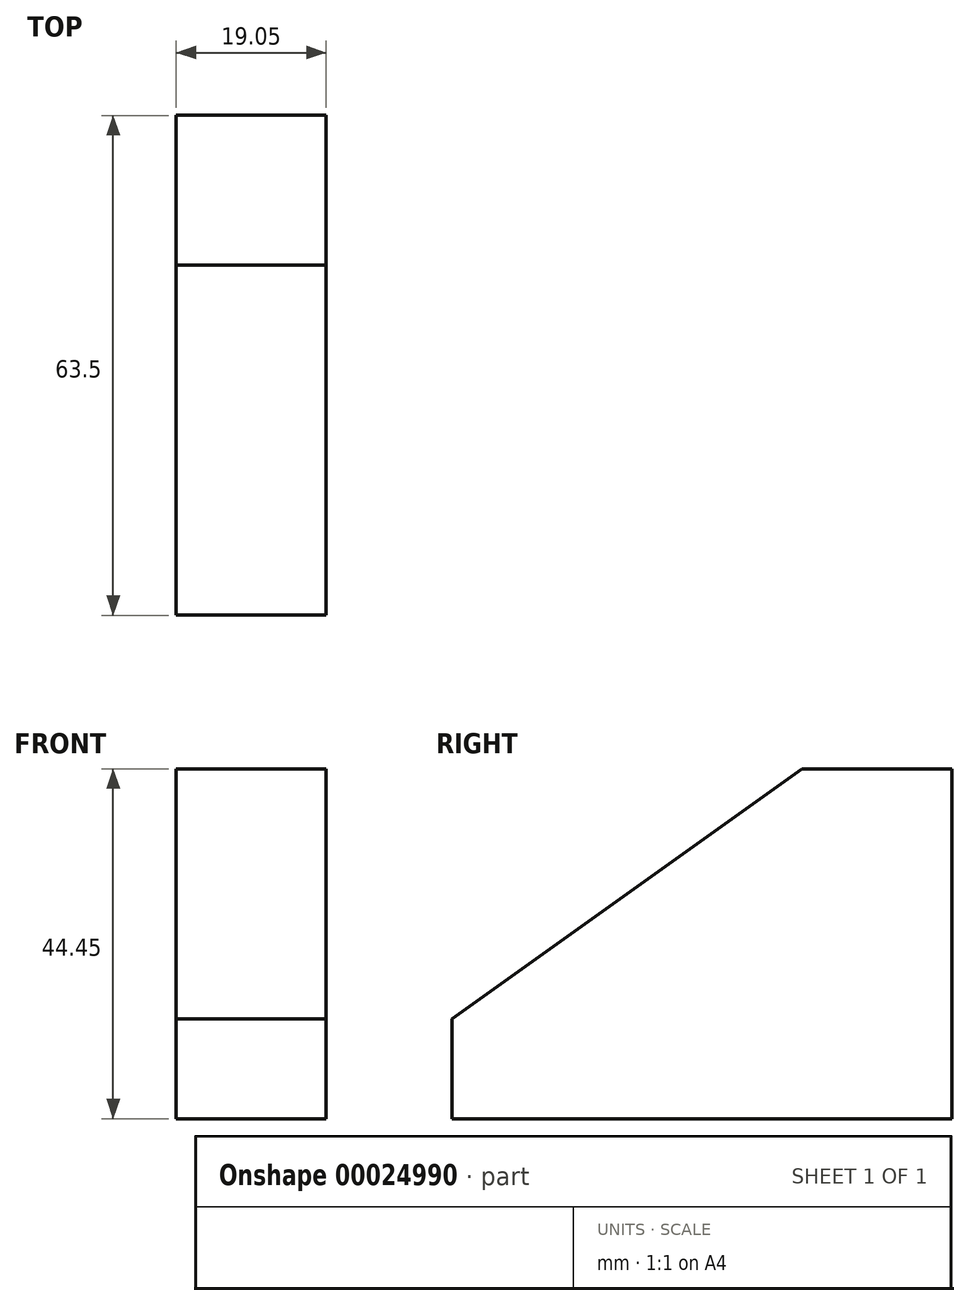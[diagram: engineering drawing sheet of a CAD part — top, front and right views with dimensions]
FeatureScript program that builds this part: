
annotation { "Feature Type Name" : "Feature", "Feature Type Description" : "" }
export const myFeature = defineFeature(function(context is Context, id is Id, definition is map)
    precondition{}
    {
        {
            var Q0;
            Q0=qCreatedBy(makeId("Right.planeOp"),FACE);
            var sketch = newSketch(context, id + "F0", { "sketchPlane" : qUnion([Q0])});
            skLineSegment(sketch, "E0", {"start": v(-84.36, 25.74) * mm, "end": v(-84.36, 13.04) * mm});
            skLineSegment(sketch, "E1", {"start": v(-84.36, 13.04) * mm, "end": v(-20.86, 13.04) * mm});
            skLineSegment(sketch, "E2", {"start": v(-20.86, 13.04) * mm, "end": v(-20.86, 57.5) * mm});
            skLineSegment(sketch, "E3", {"start": v(-20.86, 57.5) * mm, "end": v(-39.9, 57.5) * mm});
            skLineSegment(sketch, "E4", {"start": v(-39.9, 57.5) * mm, "end": v(-84.36, 25.74) * mm});
            skSolve(sketch);
        }
        {
            var Q0;
            Q0 = qSketchRegion(id + "F0", true);
            extrude(context, id + "F1", {"entities" : qUnion([Q0]), "depth" : 19.05 * mm});
        }
    });
